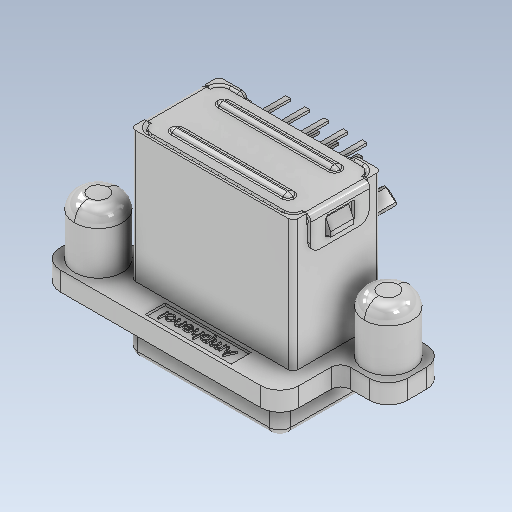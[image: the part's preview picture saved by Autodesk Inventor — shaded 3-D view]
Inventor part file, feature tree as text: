
AUTODESK INVENTOR PART (.ipt)
format: ipt  version: 2021 (Build 250183000, 183)  size: 4,710,400 bytes
history: native  units: mm
features: other x2, surface_op x1, plane x1
ambient origin geometry x8: Origin, YZ Plane, XZ Plane, XY Plane, X Axis, Y Axis, Z Axis, Center Point
bodies: Solid1 (feature_tree)
feature tree (4):
  surface_op  "Stitch Surface1"
  plane  "Work Plane1"
  other  "Composite1"
  other  "Srf1"
